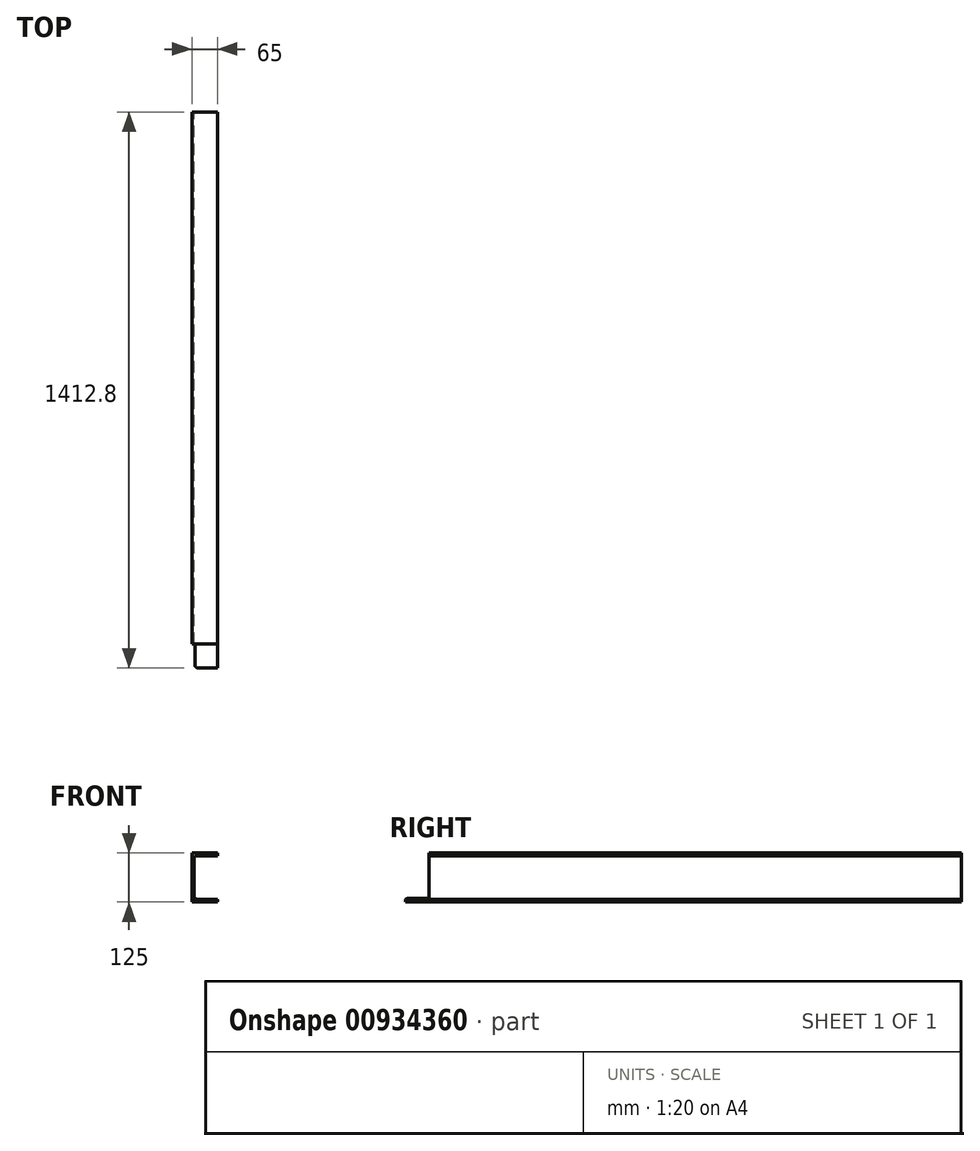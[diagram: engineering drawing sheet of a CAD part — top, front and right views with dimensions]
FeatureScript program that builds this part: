
annotation { "Feature Type Name" : "Feature", "Feature Type Description" : "" }
export const myFeature = defineFeature(function(context is Context, id is Id, definition is map)
    precondition{}
    {
        {
            var Q0;
            Q0=qCreatedBy(makeId("Front.planeOp"),FACE);
            var sketch = newSketch(context, id + "F0", { "sketchPlane" : qUnion([Q0])});
            skLineSegment(sketch, "E0", {"start": v(-25.17, -62.5) * mm, "end": v(-25.17, 62.5) * mm});
            skLineSegment(sketch, "E1", {"start": v(-25.17, 62.5) * mm, "end": v(39.83, 62.5) * mm});
            skLineSegment(sketch, "E2", {"start": v(39.83, 62.5) * mm, "end": v(39.83, 55) * mm});
            skLineSegment(sketch, "E3", {"start": v(39.83, 55) * mm, "end": v(-12.47, 55) * mm});
            skLineSegment(sketch, "E4", {"start": v(-25.17, -62.5) * mm, "end": v(39.83, -62.5) * mm});
            skLineSegment(sketch, "E5", {"start": v(39.83, -62.5) * mm, "end": v(39.83, -55) * mm});
            skLineSegment(sketch, "E6", {"start": v(39.83, -55) * mm, "end": v(-12.47, -55) * mm});
            skLineSegment(sketch, "E7", {"start": v(-20.47, -47) * mm, "end": v(-20.47, 47) * mm});
            skPoint(sketch, "E8.visualSharp", {"position": v(-20.47, 55) * mm});
            skArc(sketch, "E8.filletArc", {"start": v(-12.47, 55) * mm, "mid": v(-18.12, 52.66) * mm, "end": v(-20.47, 47) * mm});
            skPoint(sketch, "E9.visualSharp", {"position": v(-20.47, -55) * mm});
            skArc(sketch, "E9.filletArc", {"start": v(-20.47, -47) * mm, "mid": v(-18.12, -52.66) * mm, "end": v(-12.47, -55) * mm});
            skSolve(sketch);
        }
        {
            var Q0;
            Q0=makeQuery(id+"F0.imprint","IMPRINT",FACE,{"disambiguationData":[TD([[makeQuery(id+"F0.imprint","IMPRINT",EDGE,{"derivedFrom":sQuery(id+"F0.wireOp",EDGE,"E0")}),-1.0]])]});
            extrude(context, id + "F1", {"entities" : qUnion([Q0]), "depth" : 1417.5 * mm, "offsetDistance" : 25 * mm});
        }
        {
            var Q0;
            Q0=makeQuery(id+"F1.opExtrude","SWEPT_FACE",FACE,{"disambiguationData":[OSD([sQuery(id+"F0.wireOp",EDGE,"E1")])]});
            var sketch = newSketch(context, id + "F2", { "sketchPlane" : qUnion([Q0])});
            skLineSegment(sketch, "E10", {"start": v(99.83, -1417.5) * mm, "end": v(-25.17, -1417.5) * mm});
            skLineSegment(sketch, "E11", {"start": v(-25.17, -1417.5) * mm, "end": v(-25.17, -1352.5) * mm});
            skLineSegment(sketch, "E12", {"start": v(-25.17, -1352.5) * mm, "end": v(-17.67, -1352.5) * mm});
            skLineSegment(sketch, "E13", {"start": v(-17.67, -1352.5) * mm, "end": v(-17.67, -1404.8) * mm});
            skLineSegment(sketch, "E14", {"start": v(99.83, -1417.5) * mm, "end": v(99.83, -1352.5) * mm});
            skLineSegment(sketch, "E15", {"start": v(99.83, -1352.5) * mm, "end": v(92.33, -1352.5) * mm});
            skLineSegment(sketch, "E16", {"start": v(92.33, -1352.5) * mm, "end": v(92.33, -1404.8) * mm});
            skLineSegment(sketch, "E17", {"start": v(84.33, -1412.8) * mm, "end": v(-9.67, -1412.8) * mm});
            skPoint(sketch, "E18.visualSharp", {"position": v(-17.67, -1412.8) * mm});
            skArc(sketch, "E18.filletArc", {"start": v(-17.67, -1404.8) * mm, "mid": v(-15.32, -1410.46) * mm, "end": v(-9.67, -1412.8) * mm});
            skPoint(sketch, "E19.visualSharp", {"position": v(92.33, -1412.8) * mm});
            skArc(sketch, "E19.filletArc", {"start": v(84.33, -1412.8) * mm, "mid": v(89.99, -1410.46) * mm, "end": v(92.33, -1404.8) * mm});
            skSolve(sketch);
        }
        {
            var Q0;
            Q0 = qSketchRegion(id + "F2", true);
            extrude(context, id + "F3", {"entities" : qUnion([Q0]), "operationType" : NewBodyOperationType.REMOVE, "endBound" : BoundingType.THROUGH_ALL, "oppositeDirection" : true, "depth" : 25 * mm, "offsetDistance" : 25 * mm});
        }
        {
            var Q0;
            Q0=makeQuery(id+"F1.opExtrude","SWEPT_FACE",FACE,{"disambiguationData":[OSD([sQuery(id+"F0.wireOp",EDGE,"E1")])]});
            var sketch = newSketch(context, id + "F4", { "sketchPlane" : qUnion([Q0])});
            skLineSegment(sketch, "E20", {"start": v(-17.67, -1352.5) * mm, "end": v(39.83, -1352.5) * mm});
            skSolve(sketch);
        }
        {
            var Q0;
            {var subQ1=sQuery(id+"F4.wireOp",EDGE,"E20");Q0=makeQuery(id+"F4.imprint","IMPRINT",FACE,{"disambiguationData":[TD([[makeQuery(id+"F4.imprint","IMPRINT",EDGE,{"derivedFrom":subQ1}),-1.0]])]});}
            extrude(context, id + "F5", {"entities" : qUnion([Q0]), "operationType" : NewBodyOperationType.REMOVE, "oppositeDirection" : true, "depth" : 10 * mm, "offsetDistance" : 25 * mm});
        }
    });
